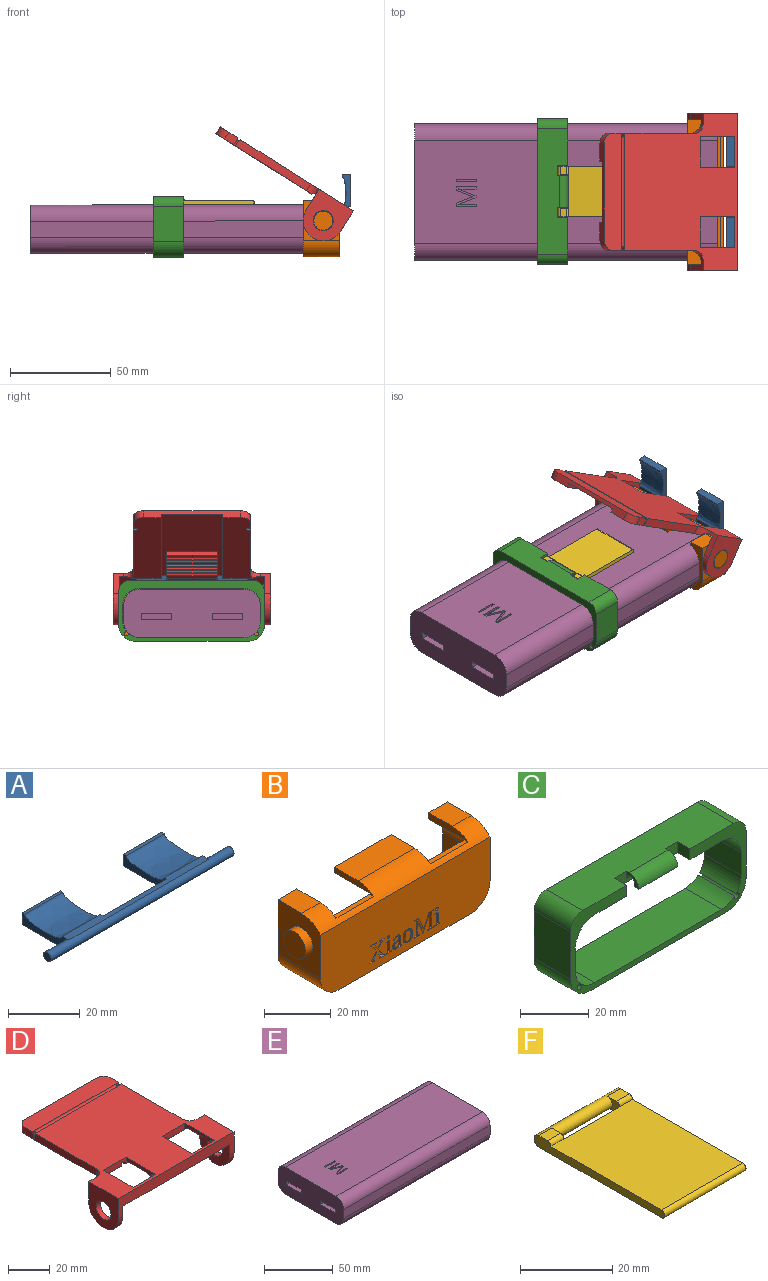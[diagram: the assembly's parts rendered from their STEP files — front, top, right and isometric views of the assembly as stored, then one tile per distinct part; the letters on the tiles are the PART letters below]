
ASSEMBLY  parts=6 mates=5
PART A: 21 faces, bbox 72x20x4 mm
  f0: plane 18.5x4mm, normal (-1,0,0), area 44.1mm2, adj f1,f10,f12,f13,f14,f15,f16,f19
  f1: plane 55x2.5mm, normal (0,0,1), area 112.5mm2, adj f0,f5,f7,f8,f9,f14,f19,f20
  f2: plane 15x1mm, normal (0,0,1), area 15mm2, adj f5,f6,f7,f20
  f3: plane 15x2.5mm, normal (0,0,-1), area 37.5mm2, adj f5,f7,f14,f17
  f4: plane 3x3mm, normal (1,0,0), area 7.1mm2, adj f14
  f5: plane 18.5x4mm, normal (1,0,0), area 44.1mm2, adj f1,f2,f3,f6,f14,f17,f18,f20
  f6: plane 15x4mm, normal (0,1,0), area 60mm2, adj f2,f5,f7,f18
  f7: plane 18.5x4mm, normal (-1,0,0), area 43.7mm2, adj f1,f2,f3,f6,f8,f14,f17,f18
  f8: plane 25x1.5mm, normal (0,1,0), area 37.5mm2, adj f1,f7,f9,f14
  f9: plane 18.5x4mm, normal (1,0,0), area 43.7mm2, adj f1,f8,f10,f12,f13,f14,f15,f16
  f10: plane 15x4mm, normal (0,1,0), area 60mm2, adj f0,f9,f12,f16
  f11: plane 3x3mm, normal (-1,0,0), area 7.1mm2, adj f14
  f12: plane 15x1mm, normal (0,0,1), area 15mm2, adj f0,f9,f10,f19
  f13: plane 15x2.5mm, normal (0,0,-1), area 37.5mm2, adj f0,f9,f14,f15
  f14: cylinder r=1.5mm len=72mm, axis (1,0,0), area 478.3mm2, adj f0,f1,f3,f4,f5,f7,f8,f9
  f15: plane 15x1mm, normal (0,-1,0), area 15mm2, adj f0,f9,f13,f16
  f16: plane 16x15mm, normal (0,0,-1), area 240mm2, adj f0,f9,f10,f15
  f17: plane 15x1mm, normal (0,-1,0), area 15mm2, adj f3,f5,f7,f18
  f18: plane 16x15mm, normal (0,0,-1), area 240mm2, adj f5,f6,f7,f17
  f19: extruded ~15x15mm, area 242.9mm2, adj f0,f1,f9,f12
  f20: extruded ~15x15mm, area 242.9mm2, adj f1,f2,f5,f7
PART B: 173 faces, bbox 78x18x28 mm
  f0: plane 72x24mm, normal (0,-1,0), area 1633.3mm2, adj f3,f8,f9,f10,f11,f12,f31,f32
  f1: plane 24x10mm, normal (0,0,1), area 240mm2, adj f3,f13,f26,f29
  f2: plane 10x8mm, normal (0,0,1), area 80mm2, adj f3,f4,f10,f28
  f3: cylinder r=10mm len=72mm, axis (1,0,0), area 436.4mm2, adj f0,f1,f2,f9,f10,f14,f25,f26
  f4: plane 72x28mm, normal (0,1,0), area 303.9mm2, adj f2,f7,f8,f9,f10,f11,f12,f14
  f5: plane 24x15mm, normal (0,0,-1), area 360mm2, adj f6,f13,f26,f29
  f6: plane 67.8x24mm, normal (0,1,0), area 1556.7mm2, adj f5,f7,f15,f16,f17,f18,f19,f20
  f7: cylinder r=8mm len=15mm, axis (0,1,0), area 156.6mm2, adj f4,f6,f15,f28
  f8: plane 56x18mm, normal (0,0,-1), area 1008mm2, adj f0,f4,f11,f12
  f9: plane 20x18mm, normal (-1,0,0), area 279.5mm2, adj f0,f3,f4,f11,f14,f23
  f10: plane 20x18mm, normal (1,0,0), area 279.5mm2, adj f0,f2,f3,f4,f12,f21
  f11: cylinder r=8mm len=18mm, axis (0,1,0), area 226.2mm2, adj f0,f4,f8,f9
  f12: cylinder r=8mm len=18mm, axis (0,-1,0), area 226.2mm2, adj f0,f4,f8,f10
  f13: plane 24x2mm, normal (0,1,0), area 48mm2, adj f1,f5,f26,f29
  f14: plane 10x8mm, normal (0,0,1), area 80mm2, adj f3,f4,f9,f25
  f15: plane 15x8mm, normal (-1,0,0), area 120mm2, adj f4,f6,f7,f18
  f16: plane 51.8x15mm, normal (0,0,1), area 777mm2, adj f4,f6,f18,f19
  f17: plane 15x8mm, normal (1,0,0), area 120mm2, adj f4,f6,f19,f20
  f18: cylinder r=8mm len=15mm, axis (0,-1,0), area 188.5mm2, adj f4,f6,f15,f16
  f19: cylinder r=8mm len=15mm, axis (0,1,0), area 188.5mm2, adj f4,f6,f16,f17
  f20: cylinder r=8mm len=15mm, axis (0,-1,0), area 156.6mm2, adj f4,f6,f17,f25
  f21: cylinder r=4.75mm len=9.5mm, axis (-1,0,0), area 89.5mm2, adj f10,f22
  f22: plane 9.5x9.5mm, normal (1,0,0), area 70.9mm2, adj f21
  f23: cylinder r=4.75mm len=9.5mm, axis (1,0,0), area 89.5mm2, adj f9,f24
  f24: plane 9.5x9.5mm, normal (-1,0,0), area 70.9mm2, adj f23
  f25: plane 16.61x2.5mm, normal (1,0,0), area 33mm2, adj f3,f4,f6,f14,f20,f27
  f26: plane 16.61x2.5mm, normal (-1,0,0), area 28.8mm2, adj f1,f3,f5,f6,f13,f27
  f27: plane 16x1.61mm, normal (0,0,1), area 25.8mm2, adj f3,f6,f25,f26
  f28: plane 16.61x2.5mm, normal (-1,0,0), area 33mm2, adj f2,f3,f4,f6,f7,f30
  f29: plane 16.61x2.5mm, normal (1,0,0), area 28.8mm2, adj f1,f3,f5,f6,f13,f30
  f30: plane 16x1.61mm, normal (0,0,1), area 25.8mm2, adj f3,f6,f28,f29
  f31: extruded ~1x0.36mm, area 0.4mm2, adj f0,f32,f38,f39
  f32: extruded ~1x0.37mm, area 0.4mm2, adj f0,f31,f33,f39
  f33: extruded ~1x0.36mm, area 0.4mm2, adj f0,f32,f34,f39
  f34: extruded ~1x0.36mm, area 0.4mm2, adj f0,f33,f35,f39
  f35: extruded ~1x0.37mm, area 0.4mm2, adj f0,f34,f36,f39
  f36: extruded ~1x0.36mm, area 0.4mm2, adj f0,f35,f37,f39
  f37: extruded ~1x0.36mm, area 0.4mm2, adj f0,f36,f38,f39
  f38: extruded ~1x0.36mm, area 0.4mm2, adj f0,f31,f37,f39
  f39: plane 1.03x1.03mm, normal (0,-1,0), area 0.8mm2, adj f31,f32,f33,f34,f35,f36,f37,f38
  f40: plane 1x0.76mm, normal (-0.15,0,-0.99), area 0.8mm2, adj f0,f41,f49,f50
  f41: plane 4.13x1mm, normal (-1,0,0), area 4.1mm2, adj f0,f40,f42,f50
  f42: plane 1.42x1mm, normal (0,0,-1), area 1.4mm2, adj f0,f41,f43,f50
  f43: plane 1x0.21mm, normal (1,0,0), area 0.2mm2, adj f0,f42,f44,f50
  f44: plane 1x0.63mm, normal (0.18,0,0.98), area 0.6mm2, adj f0,f43,f45,f50
  f45: plane 3.8x1mm, normal (1,0,0), area 3.8mm2, adj f0,f44,f46,f50
  f46: plane 1x0.76mm, normal (0.15,0,-0.99), area 0.8mm2, adj f0,f45,f47,f50
  f47: plane 1x0.21mm, normal (1,0,0), area 0.2mm2, adj f0,f46,f48,f50
  f48: plane 2.31x1mm, normal (0,0,1), area 2.3mm2, adj f0,f47,f49,f50
  f49: plane 1x0.21mm, normal (-1,0,0), area 0.2mm2, adj f0,f40,f48,f50
  f50: plane 4.46x2.31mm, normal (0,-1,0), area 4.1mm2, adj f40,f41,f42,f43,f44,f45,f46,f47
  f51: plane 1x0.17mm, normal (0,0,1), area 0.2mm2, adj f0,f52,f75,f76
  f52: plane 5.47x2.54mm, normal (-0.91,0,0.42), area 6mm2, adj f0,f51,f53,f76
  f53: plane 5.09x1mm, normal (1,0,0), area 5.1mm2, adj f0,f52,f54,f76
  f54: plane 1x0.86mm, normal (0.15,0,-0.99), area 0.9mm2, adj f0,f53,f55,f76
  f55: plane 1x0.25mm, normal (1,0,0), area 0.3mm2, adj f0,f54,f56,f76
  f56: plane 2.58x1mm, normal (0,0,1), area 2.6mm2, adj f0,f55,f57,f76
  f57: plane 1x0.25mm, normal (-1,0,0), area 0.3mm2, adj f0,f56,f58,f76
  f58: plane 1x0.82mm, normal (-0.15,0,-0.99), area 0.8mm2, adj f0,f57,f59,f76
  f59: plane 5.61x1mm, normal (-1,0,0), area 5.6mm2, adj f0,f58,f60,f76
  f60: plane 1x0.82mm, normal (-0.15,0,0.99), area 0.8mm2, adj f0,f59,f61,f76
  f61: plane 1x0.25mm, normal (-1,0,0), area 0.3mm2, adj f0,f60,f62,f76
  f62: plane 1.82x1mm, normal (0,0,-1), area 1.8mm2, adj f0,f61,f63,f76
  f63: plane 4.84x2.26mm, normal (0.91,0,-0.42), area 5.3mm2, adj f0,f62,f64,f76
  f64: plane 4.84x2.07mm, normal (-0.92,0,-0.39), area 5.3mm2, adj f0,f63,f65,f76
  f65: plane 1.93x1mm, normal (0,0,-1), area 1.9mm2, adj f0,f64,f66,f76
  f66: plane 1x0.25mm, normal (1,0,0), area 0.3mm2, adj f0,f65,f67,f76
  f67: plane 1x0.82mm, normal (0.15,0,0.99), area 0.8mm2, adj f0,f66,f68,f76
  f68: plane 5.61x1mm, normal (1,0,0), area 5.6mm2, adj f0,f67,f69,f76
  f69: plane 1x0.82mm, normal (0.15,0,-0.99), area 0.8mm2, adj f0,f68,f70,f76
  f70: plane 1x0.25mm, normal (1,0,0), area 0.3mm2, adj f0,f69,f71,f76
  f71: plane 2.17x1mm, normal (0,0,1), area 2.2mm2, adj f0,f70,f72,f76
  f72: plane 1x0.25mm, normal (-1,0,0), area 0.3mm2, adj f0,f71,f73,f76
  f73: plane 1x0.86mm, normal (-0.15,0,-0.99), area 0.9mm2, adj f0,f72,f74,f76
  f74: plane 5.09x1mm, normal (-1,0,0), area 5.1mm2, adj f0,f73,f75,f76
  f75: plane 5.47x2.33mm, normal (0.92,0,0.39), area 5.9mm2, adj f0,f51,f74,f76
  f76: plane 8.08x6.37mm, normal (0,-1,0), area 18.8mm2, adj f51,f52,f53,f54,f55,f56,f57,f58
  f77: extruded ~1x0.36mm, area 0.4mm2, adj f0,f78,f84,f85
  f78: extruded ~1x0.37mm, area 0.4mm2, adj f0,f77,f79,f85
  f79: extruded ~1x0.36mm, area 0.4mm2, adj f0,f78,f80,f85
  f80: extruded ~1x0.36mm, area 0.4mm2, adj f0,f79,f81,f85
  f81: extruded ~1x0.37mm, area 0.4mm2, adj f0,f80,f82,f85
  f82: extruded ~1x0.36mm, area 0.4mm2, adj f0,f81,f83,f85
  f83: extruded ~1x0.36mm, area 0.4mm2, adj f0,f82,f84,f85
  f84: extruded ~1x0.36mm, area 0.4mm2, adj f0,f77,f83,f85
  f85: plane 1.03x1.03mm, normal (0,-1,0), area 0.8mm2, adj f77,f78,f79,f80,f81,f82,f83,f84
  f86: extruded ~1.49x1mm, area 1.5mm2, adj f87,f100,f101,f171
  f87: extruded ~1.51x1mm, area 1.6mm2, adj f86,f88,f101,f171
  f88: extruded ~1x0.93mm, area 1.1mm2, adj f87,f89,f101,f171
  f89: extruded ~1x0.89mm, area 1mm2, adj f88,f90,f101,f171
  f90: extruded ~1.53x1mm, area 1.6mm2, adj f89,f91,f101,f171
  f91: extruded ~1.51x1mm, area 1.5mm2, adj f90,f92,f101,f171
  f92: extruded ~1x0.9mm, area 1.1mm2, adj f91,f100,f101,f171
  f93: extruded ~2.35x2.09mm, area 3.6mm2, adj f0,f94,f99,f101
  f94: extruded ~1.74x1mm, area 1.9mm2, adj f0,f93,f95,f101
  f95: extruded ~1.53x1mm, area 1.7mm2, adj f0,f94,f96,f101
  f96: extruded ~1.56x1mm, area 1.7mm2, adj f0,f95,f97,f101
  f97: extruded ~1.73x1mm, area 1.8mm2, adj f0,f96,f98,f101
  f98: extruded ~1.75x1mm, area 1.9mm2, adj f0,f97,f99,f101
  f99: extruded ~1.52x1mm, area 1.7mm2, adj f0,f93,f98,f101
  f100: extruded ~1x0.94mm, area 1.1mm2, adj f86,f92,f101,f171
  f101: plane 4.68x4.12mm, normal (0,-1,0), area 8mm2, adj f86,f87,f88,f89,f90,f91,f92,f93
  f102: plane 1x0.62mm, normal (-0.03,0,1), area 0.6mm2, adj f103,f129,f130,f172
  f103: plane 1.59x1mm, normal (1,0,0), area 1.6mm2, adj f102,f104,f130,f172
  f104: extruded ~1x0.47mm, area 0.5mm2, adj f103,f105,f130,f172
  f105: extruded ~1x0.56mm, area 0.6mm2, adj f104,f106,f130,f172
  f106: extruded ~1x0.84mm, area 1.2mm2, adj f105,f107,f130,f172
  f107: extruded ~1x0.75mm, area 0.8mm2, adj f106,f129,f130,f172
  f108: extruded ~1.08x1mm, area 1.1mm2, adj f0,f109,f128,f130
  f109: extruded ~1.35x1mm, area 1.4mm2, adj f0,f108,f110,f130
  f110: plane 1x0.97mm, normal (1,0,0), area 1mm2, adj f0,f109,f111,f130
  f111: plane 1x0.27mm, normal (0,0,1), area 0.3mm2, adj f0,f110,f112,f130
  f112: plane 1x0.56mm, normal (-0.96,0,0.28), area 0.6mm2, adj f0,f111,f113,f130
  f113: extruded ~1x0.87mm, area 0.9mm2, adj f0,f112,f114,f130
  f114: extruded ~1x0.52mm, area 0.6mm2, adj f0,f113,f115,f130
  f115: extruded ~1x0.68mm, area 0.7mm2, adj f0,f114,f116,f130
  f116: plane 1x0.7mm, normal (1,0,0), area 0.7mm2, adj f0,f115,f117,f130
  f117: plane 1x0.67mm, normal (0.03,0,-1), area 0.7mm2, adj f0,f116,f118,f130
  f118: extruded ~1.1x1mm, area 1.1mm2, adj f0,f117,f119,f130
  f119: extruded ~1x0.55mm, area 0.7mm2, adj f0,f118,f120,f130
  f120: extruded ~1x0.74mm, area 0.8mm2, adj f0,f119,f121,f130
  f121: extruded ~1.33x1.14mm, area 2mm2, adj f0,f120,f122,f130
  f122: extruded ~1.38x1mm, area 1.5mm2, adj f0,f121,f123,f130
  f123: plane 1x0.45mm, normal (0.98,0,0.2), area 0.5mm2, adj f0,f122,f124,f130
  f124: plane 1.22x1mm, normal (0,0,1), area 1.2mm2, adj f0,f123,f125,f130
  f125: plane 1x0.21mm, normal (-1,0,0), area 0.2mm2, adj f0,f124,f126,f130
  f126: plane 1x0.55mm, normal (-0.21,0,-0.98), area 0.6mm2, adj f0,f125,f127,f130
  f127: plane 3.01x1mm, normal (-1,0,0), area 3mm2, adj f0,f126,f128,f130
  f128: extruded ~1x0.92mm, area 1mm2, adj f0,f108,f127,f130
  f129: extruded ~1x0.86mm, area 0.9mm2, adj f102,f107,f130,f172
  f130: plane 4.66x3.84mm, normal (0,-1,0), area 7.6mm2, adj f102,f103,f104,f105,f106,f107,f108,f109
  f131: plane 1x0.76mm, normal (-0.15,0,-0.99), area 0.8mm2, adj f0,f132,f140,f141
  f132: plane 4.13x1mm, normal (-1,0,0), area 4.1mm2, adj f0,f131,f133,f141
  f133: plane 1.42x1mm, normal (0,0,-1), area 1.4mm2, adj f0,f132,f134,f141
  f134: plane 1x0.21mm, normal (1,0,0), area 0.2mm2, adj f0,f133,f135,f141
  f135: plane 1x0.63mm, normal (0.18,0,0.98), area 0.6mm2, adj f0,f134,f136,f141
  f136: plane 3.8x1mm, normal (1,0,0), area 3.8mm2, adj f0,f135,f137,f141
  f137: plane 1x0.76mm, normal (0.15,0,-0.99), area 0.8mm2, adj f0,f136,f138,f141
  f138: plane 1x0.21mm, normal (1,0,0), area 0.2mm2, adj f0,f137,f139,f141
  f139: plane 2.31x1mm, normal (0,0,1), area 2.3mm2, adj f0,f138,f140,f141
  f140: plane 1x0.21mm, normal (-1,0,0), area 0.2mm2, adj f0,f131,f139,f141
  f141: plane 4.46x2.31mm, normal (0,-1,0), area 4.1mm2, adj f131,f132,f133,f134,f135,f136,f137,f138
  f142: plane 1x0.79mm, normal (-0.16,0,-0.99), area 0.8mm2, adj f0,f143,f169,f170
  f143: plane 2.47x1.85mm, normal (-0.8,0,0.6), area 3.1mm2, adj f0,f142,f144,f170
  f144: plane 2.47x1.67mm, normal (0.83,0,0.56), area 3mm2, adj f0,f143,f145,f170
  f145: plane 1x0.81mm, normal (0.16,0,-0.99), area 0.8mm2, adj f0,f144,f146,f170
  f146: plane 1x0.25mm, normal (1,0,0), area 0.3mm2, adj f0,f145,f147,f170
  f147: plane 2.63x1mm, normal (0,0,1), area 2.6mm2, adj f0,f146,f148,f170
  f148: plane 1x0.25mm, normal (-1,0,0), area 0.3mm2, adj f0,f147,f149,f170
  f149: plane 1x0.72mm, normal (-0.17,0,-0.98), area 0.7mm2, adj f0,f148,f150,f170
  f150: plane 3.23x2.19mm, normal (-0.83,0,-0.56), area 3.9mm2, adj f0,f149,f151,f170
  f151: plane 2.38x1.79mm, normal (-0.8,0,0.6), area 3mm2, adj f0,f150,f152,f170
  f152: plane 1x0.7mm, normal (-0.17,0,0.98), area 0.7mm2, adj f0,f151,f153,f170
  f153: plane 1x0.25mm, normal (-1,0,0), area 0.3mm2, adj f0,f152,f154,f170
  f154: plane 2.08x1mm, normal (0,0,-1), area 2.1mm2, adj f0,f153,f155,f170
  f155: plane 1x0.25mm, normal (1,0,0), area 0.3mm2, adj f0,f154,f156,f170
  f156: plane 1x0.79mm, normal (0.15,0,0.99), area 0.8mm2, adj f0,f155,f157,f170
  f157: plane 1.97x1.48mm, normal (0.8,0,-0.6), area 2.5mm2, adj f0,f156,f158,f170
  f158: plane 1.97x1.32mm, normal (-0.83,0,-0.56), area 2.4mm2, adj f0,f157,f159,f170
  f159: plane 1x0.81mm, normal (-0.15,0,0.99), area 0.8mm2, adj f0,f158,f160,f170
  f160: plane 1x0.25mm, normal (-1,0,0), area 0.3mm2, adj f0,f159,f161,f170
  f161: plane 2.63x1mm, normal (0,0,-1), area 2.6mm2, adj f0,f160,f162,f170
  f162: plane 1x0.25mm, normal (1,0,0), area 0.3mm2, adj f0,f161,f163,f170
  f163: plane 1x0.72mm, normal (0.17,0,0.99), area 0.7mm2, adj f0,f162,f164,f170
  f164: plane 2.73x1.85mm, normal (0.83,0,0.56), area 3.3mm2, adj f0,f163,f165,f170
  f165: plane 2.88x2.16mm, normal (0.8,0,-0.6), area 3.6mm2, adj f0,f164,f166,f170
  f166: plane 1x0.7mm, normal (0.18,0,-0.98), area 0.7mm2, adj f0,f165,f167,f170
  f167: plane 1x0.25mm, normal (1,0,0), area 0.3mm2, adj f0,f166,f168,f170
  f168: plane 2.08x1mm, normal (0,0,1), area 2.1mm2, adj f0,f167,f169,f170
  f169: plane 1x0.25mm, normal (-1,0,0), area 0.3mm2, adj f0,f142,f168,f170
  f170: plane 6.63x6.37mm, normal (0,-1,0), area 12.2mm2, adj f142,f143,f144,f145,f146,f147,f148,f149
  f171: plane 3.92x2.41mm, normal (0,-1,0), area 8mm2, adj f86,f87,f88,f89,f90,f91,f92,f100
  f172: plane 1.85x1.71mm, normal (0,-1,0), area 2.8mm2, adj f102,f103,f104,f105,f106,f107,f129
PART C: 32 faces, bbox 72x15x30 mm
  f0: cylinder r=8mm len=15mm, axis (0,-1,0), area 88mm2, adj f5,f15,f29,f31
  f1: cylinder r=8mm len=15mm, axis (0,-1,0), area 88mm2, adj f5,f17,f29,f30
  f2: plane 16x1.9mm, normal (0,0,-1), area 30.4mm2, adj f3,f22,f23,f26
  f3: plane 5x3.9mm, normal (1,0,0), area 7.9mm2, adj f2,f4,f19,f23,f24,f25,f26
  f4: plane 26x3.9mm, normal (0,-1,0), area 61.4mm2, adj f3,f13,f19,f22,f25,f27,f28
  f5: plane 72x30mm, normal (0,1,0), area 525mm2, adj f0,f1,f6,f7,f8,f9,f10,f11
  f6: plane 17x15mm, normal (-1,0,0), area 255mm2, adj f5,f9,f20,f29
  f7: plane 56x15mm, normal (0,0,-1), area 840mm2, adj f5,f9,f10,f29
  f8: plane 17x15mm, normal (1,0,0), area 255mm2, adj f5,f10,f21,f29
  f9: cylinder r=8mm len=15mm, axis (0,1,0), area 188.5mm2, adj f5,f6,f7,f29
  f10: cylinder r=8mm len=15mm, axis (0,-1,0), area 188.5mm2, adj f5,f7,f8,f29
  f11: plane 15x8.2mm, normal (-1,0,0), area 123mm2, adj f5,f12,f18,f29
  f12: cylinder r=8mm len=15mm, axis (0,-1,0), area 188.5mm2, adj f5,f11,f13,f29
  f13: plane 52x15mm, normal (0,0,-1), area 650mm2, adj f4,f5,f12,f14,f27,f28,f29
  f14: cylinder r=8mm len=15mm, axis (0,-1,0), area 188.5mm2, adj f5,f13,f15,f29
  f15: plane 15x8.2mm, normal (1,0,0), area 123mm2, adj f0,f5,f14,f29
  f16: cylinder r=8mm len=15mm, axis (0,-1,0), area 88mm2, adj f5,f17,f29,f31
  f17: plane 52x15mm, normal (0,0,1), area 780mm2, adj f1,f5,f16,f29
  f18: cylinder r=8mm len=15mm, axis (0,-1,0), area 88mm2, adj f5,f11,f29,f30
  f19: plane 62x15mm, normal (0,0,1), area 816mm2, adj f3,f4,f5,f20,f21,f22,f26,f27
  f20: cylinder r=5mm len=15mm, axis (0,-1,0), area 117.8mm2, adj f5,f6,f19,f29
  f21: cylinder r=5mm len=15mm, axis (0,1,0), area 117.8mm2, adj f5,f8,f19,f29
  f22: plane 5x3.9mm, normal (-1,0,0), area 7.9mm2, adj f2,f4,f19,f23,f24,f25,f26
  f23: plane 16x1.4mm, normal (0,1,0), area 22.4mm2, adj f2,f3,f22,f24
  f24: cylinder r=1.6mm len=16mm, axis (-1,0,0), area 39.4mm2, adj f3,f22,f23,f25
  f25: cylinder r=1.6mm len=16mm, axis (-1,0,0), area 39.4mm2, adj f3,f4,f22,f24
  f26: cylinder r=4mm len=16mm, axis (1,0,0), area 98.9mm2, adj f2,f3,f19,f22
  f27: plane 5x3.9mm, normal (1,0,0), area 19.5mm2, adj f4,f13,f19,f29
  f28: plane 5x3.9mm, normal (-1,0,0), area 19.5mm2, adj f4,f13,f19,f29
  f29: plane 72x30mm, normal (0,-1,0), area 423.6mm2, adj f0,f1,f6,f7,f8,f9,f10,f11
  f30: cylinder r=1mm len=15mm, axis (0,-1,0), area 81.5mm2, adj f1,f5,f18,f29
  f31: cylinder r=1mm len=15mm, axis (0,-1,0), area 81.5mm2, adj f0,f5,f16,f29
PART D: 76 faces, bbox 78x78x22 mm
  f0: cylinder r=10mm len=2.12mm, axis (1,0,0), area 3mm2, adj f1,f26,f30,f66
  f1: plane 3.37x2.54mm, normal (-1,0,0), area 2.7mm2, adj f0,f26,f27,f66
  f2: cylinder r=10mm len=2.12mm, axis (-1,0,0), area 3mm2, adj f3,f12,f65,f66
  f3: plane 3.37x2.54mm, normal (1,0,0), area 2.7mm2, adj f2,f27,f65,f66
  f4: plane 5.56x4mm, normal (-1,0,0), area 21.9mm2, adj f9,f10,f43,f52,f74
  f5: plane 5.56x4mm, normal (1,0,0), area 21.9mm2, adj f6,f10,f31,f51,f75
  f6: cylinder r=1mm len=0.9mm, axis (-1,0,0), area 0.4mm2, adj f5,f10,f75
  f7: cylinder r=1mm len=56.2mm, axis (-1,0,0), area 172.6mm2, adj f10,f18,f74,f75
  f8: cylinder r=1mm len=0.9mm, axis (-1,0,0), area 0.4mm2, adj f11,f18,f74
  f9: cylinder r=1mm len=0.9mm, axis (-1,0,0), area 0.4mm2, adj f4,f10,f74
  f10: plane 58x10mm, normal (0,0,1), area 569.3mm2, adj f4,f5,f6,f7,f9,f32,f51,f52
  f11: plane 41.56x4mm, normal (-1,0,0), area 165.9mm2, adj f8,f18,f42,f43,f74
  f12: plane 21x20mm, normal (1,0,0), area 269.1mm2, adj f2,f16,f29,f44,f45,f49,f53,f64
  f13: cylinder r=10mm len=24.5mm, axis (-1,0,0), area 133.9mm2, adj f15,f23,f68,f71
  f14: cylinder r=10mm len=8.5mm, axis (-1,0,0), area 46.5mm2, adj f17,f24,f30,f69
  f15: plane 68x30.5mm, normal (0,0,-1), area 1479.4mm2, adj f13,f19,f20,f32,f39,f54,f55,f56
  f16: plane 10x8.5mm, normal (0,0,-1), area 85mm2, adj f12,f22,f29,f44,f72
  f17: plane 10x8.5mm, normal (0,0,-1), area 85mm2, adj f14,f21,f30,f47,f69
  f18: plane 78x66mm, normal (0,0,1), area 3628.7mm2, adj f7,f8,f11,f27,f28,f40,f41,f42
  f19: plane 56.4x2mm, normal (-1,0,0), area 112.7mm2, adj f15,f21,f31,f32,f67
  f20: plane 56.4x2mm, normal (1,0,0), area 112.7mm2, adj f15,f22,f32,f43,f70
  f21: plane 18.75x2mm, normal (0,-0.71,-0.71), area 17.4mm2, adj f17,f19,f31,f41,f67,f69
  f22: plane 18.75x2mm, normal (0,-0.71,-0.71), area 17.4mm2, adj f16,f20,f42,f43,f70,f72
  f23: plane 24.5x0.86mm, normal (0,-1,0), area 21mm2, adj f13,f25,f68,f71
  f24: plane 8.5x0.86mm, normal (0,-1,0), area 7.3mm2, adj f14,f26,f30,f69
  f25: cylinder r=1.6mm len=24.5mm, axis (-1,0,0), area 123.2mm2, adj f23,f27,f68,f71
  f26: cylinder r=1.6mm len=8.5mm, axis (-1,0,0), area 46.2mm2, adj f0,f1,f24,f27,f30,f69
  f27: plane 70x5.97mm, normal (0,1,0), area 315.5mm2, adj f1,f3,f18,f25,f26,f65,f66,f68
  f28: plane 22x20mm, normal (-1,0,0), area 318.5mm2, adj f18,f44,f45,f49,f53
  f29: cylinder r=10mm len=8.5mm, axis (-1,0,0), area 46.5mm2, adj f12,f16,f64,f72
  f30: plane 21x20mm, normal (-1,0,0), area 269.1mm2, adj f0,f14,f17,f24,f26,f46,f47,f48
  f31: plane 56x14.75mm, normal (0,0,-1), area 762.5mm2, adj f5,f19,f21,f32,f41,f50,f51,f75
  f32: plane 48x4mm, normal (0,1,0), area 131mm2, adj f10,f15,f19,f20,f31,f43,f51,f52
  f33: plane 25x2mm, normal (0,0,-1), area 50mm2, adj f39,f55,f56,f63
  f34: plane 25x1mm, normal (0,0,-1), area 25mm2, adj f39,f55,f62,f63
  f35: plane 25x1mm, normal (0,0,-1), area 25mm2, adj f39,f55,f61,f62
  f36: plane 25x1mm, normal (0,0,-1), area 25mm2, adj f39,f55,f60,f61
  f37: plane 25x1mm, normal (0,0,-1), area 25mm2, adj f39,f55,f59,f60
  f38: plane 25x1mm, normal (0,0,-1), area 25mm2, adj f39,f55,f58,f59
  f39: plane 21x2mm, normal (-1,0,0), area 32.6mm2, adj f15,f33,f34,f35,f36,f37,f38,f54
  f40: plane 22x20mm, normal (1,0,0), area 318.5mm2, adj f18,f46,f47,f48,f53
  f41: cylinder r=5mm len=5mm, axis (0,0,-1), area 25.3mm2, adj f18,f21,f31,f47,f50
  f42: cylinder r=5mm len=5mm, axis (0,0,-1), area 25.3mm2, adj f11,f18,f22,f43,f44
  f43: plane 56x14.75mm, normal (0,0,-1), area 762.5mm2, adj f4,f11,f20,f22,f32,f42,f52,f74
  f44: plane 12x5mm, normal (0,1,0), area 40mm2, adj f12,f16,f18,f28,f42,f45
  f45: cylinder r=10mm len=20mm, axis (-1,0,0), area 94.2mm2, adj f12,f28,f44,f53
  f46: cylinder r=10mm len=20mm, axis (1,0,0), area 94.2mm2, adj f30,f40,f47,f53
  f47: plane 12x5mm, normal (0,1,0), area 40mm2, adj f17,f18,f30,f40,f41,f46
  f48: cylinder r=5mm len=10mm, axis (-1,0,0), area 94.2mm2, adj f30,f40
  f49: cylinder r=5mm len=10mm, axis (-1,0,0), area 94.2mm2, adj f12,f28
  f50: plane 41.56x4mm, normal (1,0,0), area 165.9mm2, adj f18,f31,f41,f73,f75
  f51: cylinder r=5mm len=5mm, axis (0,0,-1), area 31.4mm2, adj f5,f10,f31,f32
  f52: cylinder r=5mm len=5mm, axis (0,0,1), area 31.4mm2, adj f4,f10,f32,f43
  f53: plane 78x12mm, normal (0,-1,0), area 502.2mm2, adj f12,f18,f28,f30,f40,f45,f46,f66
  f54: plane 25x2mm, normal (0,1,0), area 50mm2, adj f15,f39,f55,f57
  f55: plane 21x2mm, normal (1,0,0), area 32.6mm2, adj f15,f33,f34,f35,f36,f37,f38,f54
  f56: plane 25x2mm, normal (0,-1,0), area 50mm2, adj f15,f33,f39,f55
  f57: plane 25x2mm, normal (0,0,-1), area 50mm2, adj f39,f54,f55,f58
  f58: cylinder r=1mm len=25mm, axis (-1,0,0), area 78.5mm2, adj f38,f39,f55,f57
  f59: cylinder r=1mm len=25mm, axis (-1,0,0), area 78.5mm2, adj f37,f38,f39,f55
  f60: cylinder r=1mm len=25mm, axis (-1,0,0), area 78.5mm2, adj f36,f37,f39,f55
  f61: cylinder r=1mm len=25mm, axis (-1,0,0), area 78.5mm2, adj f35,f36,f39,f55
  f62: cylinder r=1mm len=25mm, axis (-1,0,0), area 78.5mm2, adj f34,f35,f39,f55
  f63: cylinder r=1mm len=25mm, axis (-1,0,0), area 78.5mm2, adj f33,f34,f39,f55
  f64: plane 8.5x0.86mm, normal (0,-1,0), area 7.3mm2, adj f12,f29,f65,f72
  f65: cylinder r=1.6mm len=8.5mm, axis (-1,0,0), area 46.2mm2, adj f2,f3,f12,f27,f64,f72
  f66: plane 72x2.02mm, normal (0,0,-1), area 116.2mm2, adj f0,f1,f2,f3,f12,f27,f30,f53
  f67: plane 15.25x3.6mm, normal (0,-1,0), area 50.1mm2, adj f15,f18,f19,f21,f68,f69
  f68: plane 20x3.46mm, normal (1,0,0), area 40.3mm2, adj f13,f15,f18,f23,f25,f27,f67
  f69: plane 20x3.6mm, normal (-1,0,0), area 41.6mm2, adj f14,f17,f18,f21,f24,f26,f27,f67
  f70: plane 15.25x3.6mm, normal (0,-1,0), area 50.1mm2, adj f15,f18,f20,f22,f71,f72
  f71: plane 20x3.46mm, normal (-1,0,0), area 40.3mm2, adj f13,f15,f18,f23,f25,f27,f70
  f72: plane 20x3.6mm, normal (1,0,0), area 41.6mm2, adj f16,f18,f22,f27,f29,f64,f65,f70
  f73: cylinder r=1mm len=0.9mm, axis (-1,0,0), area 0.4mm2, adj f18,f50,f75
  f74: cylinder r=1mm len=4mm, axis (0,0,1), area 18.4mm2, adj f4,f7,f8,f9,f11,f43
  f75: cylinder r=1mm len=4mm, axis (0,0,1), area 18.4mm2, adj f5,f6,f7,f31,f50,f73
PART E: 44 faces, bbox 150x67.5x24 mm
  f0: plane 67.5x24mm, normal (-1,0,0), area 1467.1mm2, adj f1,f2,f3,f5,f6,f7,f8,f9
  f1: plane 150x51.5mm, normal (0,0,1), area 7671.5mm2, adj f0,f4,f8,f9,f10,f11,f12,f13
  f2: plane 150x8mm, normal (0,1,0), area 1200mm2, adj f0,f4,f7,f9
  f3: plane 150x8mm, normal (0,-1,0), area 1200mm2, adj f0,f4,f6,f8
  f4: plane 67.5x24mm, normal (1,0,0), area 1565.1mm2, adj f1,f2,f3,f5,f6,f7,f8,f9
  f5: plane 150x51.5mm, normal (0,0,-1), area 7725mm2, adj f0,f4,f6,f7
  f6: cylinder r=8mm len=150mm, axis (1,0,0), area 1885mm2, adj f0,f3,f4,f5
  f7: cylinder r=8mm len=150mm, axis (-1,0,0), area 1885mm2, adj f0,f2,f4,f5
  f8: cylinder r=8mm len=150mm, axis (-1,0,0), area 1885mm2, adj f0,f1,f3,f4
  f9: cylinder r=8mm len=150mm, axis (1,0,0), area 1885mm2, adj f0,f1,f2,f4
  f10: plane 9.92x1mm, normal (0,1,0), area 9.9mm2, adj f1,f11,f13,f14
  f11: plane 1.15x1mm, normal (-1,0,0), area 1.2mm2, adj f1,f10,f12,f14
  f12: plane 9.92x1mm, normal (0,-1,0), area 9.9mm2, adj f1,f11,f13,f14
  f13: plane 1.15x1mm, normal (1,0,0), area 1.2mm2, adj f1,f10,f12,f14
  f14: plane 9.92x1.15mm, normal (0,0,1), area 11.4mm2, adj f10,f11,f12,f13
  f15: plane 8.79x3.36mm, normal (-0.36,0.93,0), area 9.4mm2, adj f1,f16,f32,f33
  f16: plane 1x0.93mm, normal (-1,0,0), area 0.9mm2, adj f1,f15,f17,f33
  f17: plane 8.78x3.39mm, normal (-0.36,-0.93,0), area 9.4mm2, adj f1,f16,f18,f33
  f18: plane 1x0.05mm, normal (-1,0,0), area 0.1mm2, adj f1,f17,f19,f33
  f19: extruded ~2.39x1mm, area 2.4mm2, adj f1,f18,f20,f33
  f20: plane 6.39x1mm, normal (0,1,0), area 6.4mm2, adj f1,f19,f21,f33
  f21: plane 1.15x1mm, normal (-1,0,0), area 1.2mm2, adj f1,f20,f22,f33
  f22: plane 9.92x1mm, normal (0,-1,0), area 9.9mm2, adj f1,f21,f23,f33
  f23: plane 1.72x1mm, normal (1,0,0), area 1.7mm2, adj f1,f22,f24,f33
  f24: plane 8.18x3.17mm, normal (0.36,0.93,0), area 8.8mm2, adj f1,f23,f25,f33
  f25: plane 1x0.05mm, normal (1,0,0), area 0.1mm2, adj f1,f24,f26,f33
  f26: plane 8.18x3.14mm, normal (0.36,-0.93,0), area 8.8mm2, adj f1,f25,f27,f33
  f27: plane 1.74x1mm, normal (1,0,0), area 1.7mm2, adj f1,f26,f28,f33
  f28: plane 9.92x1mm, normal (0,1,0), area 9.9mm2, adj f1,f27,f29,f33
  f29: plane 1.07x1mm, normal (-1,0,0), area 1.1mm2, adj f1,f28,f30,f33
  f30: plane 6.31x1mm, normal (0,-1,0), area 6.3mm2, adj f1,f29,f31,f33
  f31: extruded ~2.48x1mm, area 2.5mm2, adj f1,f30,f32,f33
  f32: plane 1x0.05mm, normal (-1,0,0), area 0.1mm2, adj f1,f15,f31,f33
  f33: plane 9.92x9.82mm, normal (0,0,1), area 42mm2, adj f15,f16,f17,f18,f19,f20,f21,f22
  f34: plane 15x10mm, normal (0,0,-1), area 150mm2, adj f0,f35,f37,f38
  f35: plane 10x3.26mm, normal (0,-1,0), area 32.6mm2, adj f0,f34,f36,f38
  f36: plane 15x10mm, normal (0,0,1), area 150mm2, adj f0,f35,f37,f38
  f37: plane 10x3.26mm, normal (0,1,0), area 32.6mm2, adj f0,f34,f36,f38
  f38: plane 15x3.26mm, normal (-1,0,0), area 49mm2, adj f34,f35,f36,f37
  f39: plane 10x3.26mm, normal (0,-1,0), area 32.6mm2, adj f0,f40,f42,f43
  f40: plane 15x10mm, normal (0,0,1), area 150mm2, adj f0,f39,f41,f43
  f41: plane 10x3.26mm, normal (0,1,0), area 32.6mm2, adj f0,f40,f42,f43
  f42: plane 15x10mm, normal (0,0,-1), area 150mm2, adj f0,f39,f41,f43
  f43: plane 15x3.26mm, normal (-1,0,0), area 49mm2, adj f39,f40,f41,f42
PART F: 13 faces, bbox 25x40x3 mm
  f0: plane 17x2mm, normal (0,1,0), area 34mm2, adj f5,f6,f7,f9
  f1: plane 40x3mm, normal (1,0,0), area 83.6mm2, adj f3,f7,f8,f9,f10,f12
  f2: plane 4x2.7mm, normal (0,0,1), area 10.8mm2, adj f4,f5,f8,f11
  f3: plane 4x2.7mm, normal (0,0,1), area 10.8mm2, adj f1,f6,f8,f10
  f4: plane 40x3mm, normal (-1,0,0), area 83.6mm2, adj f2,f7,f8,f9,f11,f12
  f5: plane 3.7x3mm, normal (1,0,0), area 7.4mm2, adj f0,f2,f7,f8,f11
  f6: plane 3.7x3mm, normal (-1,0,0), area 7.4mm2, adj f0,f3,f7,f8,f10
  f7: plane 37.5x25mm, normal (0,0,-1), area 874.6mm2, adj f0,f1,f4,f5,f6,f8,f12
  f8: cylinder r=1.5mm len=25mm, axis (-1,0,0), area 197.9mm2, adj f1,f2,f3,f4,f5,f6,f7
  f9: plane 33.8x25mm, normal (0,0,1), area 845mm2, adj f0,f1,f4,f10,f11,f12
  f10: cylinder r=1mm len=4mm, axis (1,0,0), area 6.3mm2, adj f1,f3,f6,f9
  f11: cylinder r=1mm len=4mm, axis (1,0,0), area 6.3mm2, adj f2,f4,f5,f9
  f12: cylinder r=1mm len=25mm, axis (1,0,0), area 78.5mm2, adj f1,f4,f7,f9
PLACE A rot(axis=(0.58,-0.58,-0.58),120deg) t=(119.59,74.63,-29.98)mm
PLACE B rot(axis=(0,0,1),90deg) t=(97.33,74.63,-46.8)mm
PLACE C rot(axis=(0,0,1),90deg) t=(23.23,74.88,-46.91)mm
PLACE D rot(axis=(0.27,0.27,0.93),94.4deg) t=(88.16,74.63,-18.84)mm
PLACE E rot(axis=(0,-1,0),0.1deg) t=(32.96,74.63,-59)mm fixed
PLACE F rot(axis=(0,0,1),90deg) t=(53.22,74.88,-34.87)mm
MATE slider C.f0 <-> E.f6  axis (1,0,0) through (30.74,48.88,-51)mm
MATE revolute D.f45 <-> B.f3  axis (0,1,0) through (107.33,38.63,-42.79)mm
MATE revolute A.f14 <-> D.f25  axis (0,-1,0) through (118.1,74.63,-38.48)mm
MATE fastened B.f6 <-> E.f4  axis (-1,0,0) through (112.33,74.63,-46.9)mm
MATE revolute F.f8 <-> C.f24  axis (0,-1,0) through (34.72,74.88,-33.39)mm
